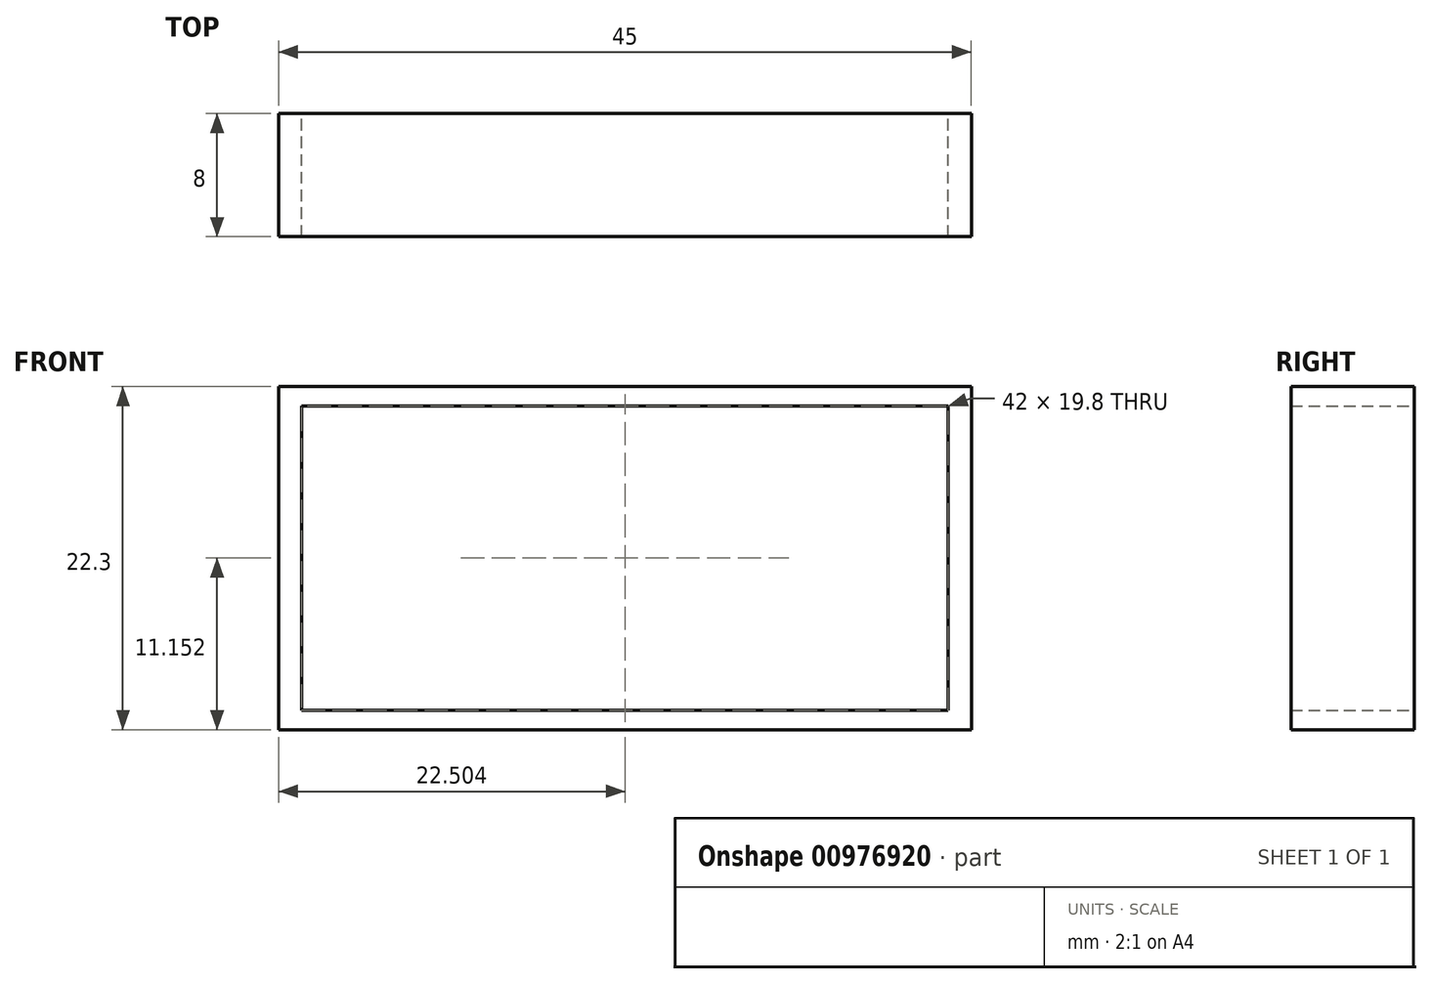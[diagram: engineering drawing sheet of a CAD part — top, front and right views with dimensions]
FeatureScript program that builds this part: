
annotation { "Feature Type Name" : "Feature", "Feature Type Description" : "" }
export const myFeature = defineFeature(function(context is Context, id is Id, definition is map)
    precondition{}
    {
        {
            var Q0;
            Q0=qCreatedBy(makeId("Front.planeOp"),FACE);
            var sketch = newSketch(context, id + "F0", { "sketchPlane" : qUnion([Q0])});
            skLineSegment(sketch, "E0.bottom", {"start": v(-23.38, 10.3) * mm, "end": v(21.62, 10.3) * mm});
            skLineSegment(sketch, "E0.top", {"start": v(-23.38, -12) * mm, "end": v(21.62, -12) * mm});
            skLineSegment(sketch, "E0.left", {"start": v(-23.38, 10.3) * mm, "end": v(-23.38, -12) * mm});
            skLineSegment(sketch, "E0.right", {"start": v(21.62, 10.3) * mm, "end": v(21.62, -12) * mm});
            skLineSegment(sketch, "E1.bottom", {"start": v(-21.88, 9.04) * mm, "end": v(20.12, 9.04) * mm});
            skLineSegment(sketch, "E1.top", {"start": v(-21.88, -10.76) * mm, "end": v(20.12, -10.76) * mm});
            skLineSegment(sketch, "E1.left", {"start": v(-21.88, 9.04) * mm, "end": v(-21.88, -10.76) * mm});
            skLineSegment(sketch, "E1.right", {"start": v(20.12, 9.04) * mm, "end": v(20.12, -10.76) * mm});
            skSolve(sketch);
        }
        {
            var Q0;
            Q0 = qSketchRegion(id + "F0", true);
            extrude(context, id + "F1", {"entities" : qUnion([Q0]), "depth" : 8 * mm, "offsetDistance" : 25 * mm});
        }
    });
